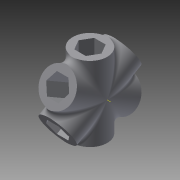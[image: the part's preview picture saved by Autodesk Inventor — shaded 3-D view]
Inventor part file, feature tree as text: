
AUTODESK INVENTOR PART (.ipt)
format: ipt  version: 2015 SP1 (Build 190203100, 203)  size: 325,632 bytes
history: native  units: mm
features: other x7, extrude x5, sketch x5, projected_geometry x3, pattern_circular x2, fillet x1
ambient origin geometry x8: Origin, YZ Plane, XZ Plane, XY Plane, X Axis, Y Axis, Z Axis, Center Point
bodies: Body1 (feature_tree)
feature tree (23):
  other  "Sólido1"
  extrude  "Extrusión1"  Depth=12.0mm
  extrude  "Extrusión2"  Depth=6.0mm TaperAngle=0.0deg
  other  "Eje de trabajo1"
  other  "Eje de trabajo2"
  pattern_circular  "Patrón circular1"  Count=4 Angle=360.0deg
  pattern_circular  "Patrón circular2"  Count=6 Angle=360.0deg
  extrude  "Extrusión3"  Depth=45.0mm TaperAngle=0.0deg
  extrude  "Extrusión4"  Depth=2.0mm
  extrude  "Extrusión5"  [1 undecoded]
  fillet  "Empalme1"  [1 undecoded]
  sketch  "Boceto1"  dims[d0=8.0mm d1=12.0mm]
  sketch  "Boceto2"  dims[d2=7.0mm d3=0.0mm d4=6.0mm d5=0.0mm d6=40.0mm d7=360.0deg d9=60.0mm d10=360.0deg]
  other  "Punto de trabajo1"
  other  "Eje de trabajo3"
  other  "Eje de trabajo4"
  other  "Eje de trabajo5"
  sketch  "Boceto3"  dims[d12=45.0mm d13=0.0mm d14=45.0mm d15=0.0mm]
  projected_geometry  "Contorno proyectado1"
  sketch  "Boceto4"  dims[d16=45.0mm d17=0.0mm d18=2.0mm]
  projected_geometry  "Contorno proyectado2"
  sketch  "Boceto5"
  projected_geometry  "Contorno proyectado3"
note: 2 required parameter values undecoded (feature->parameter linkage not recoverable at this tier; creation-order binding heuristic only, values carry confidence <= 0.55)
